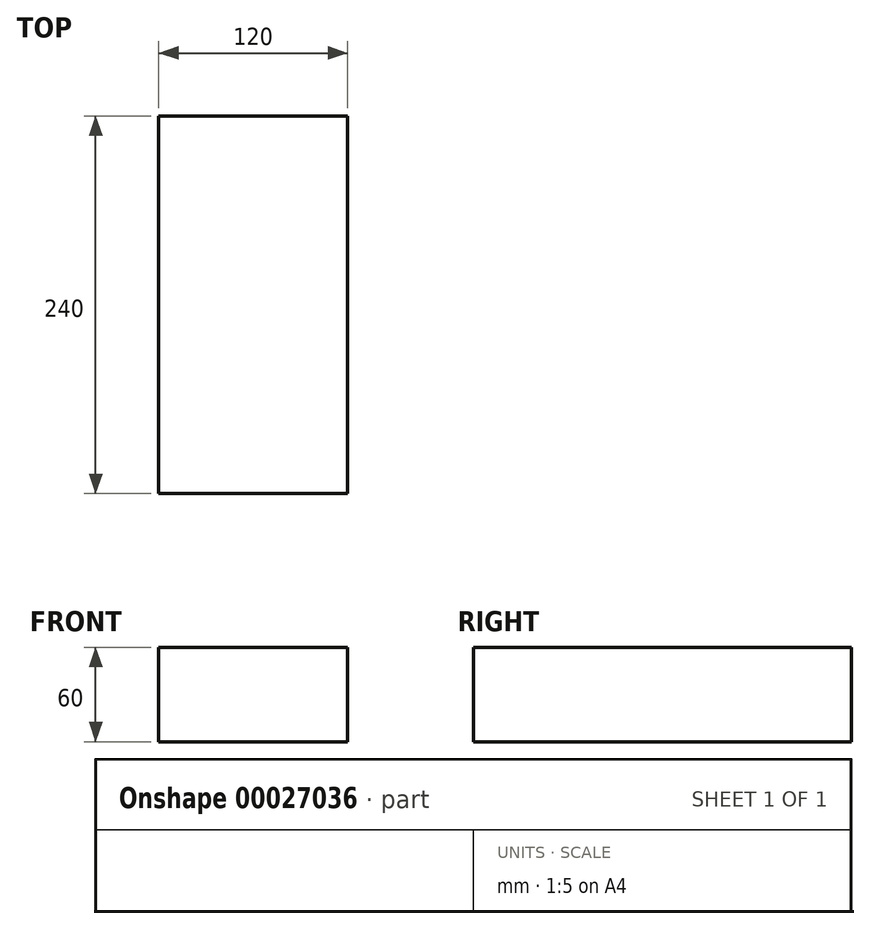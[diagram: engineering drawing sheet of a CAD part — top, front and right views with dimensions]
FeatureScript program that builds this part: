
annotation { "Feature Type Name" : "Feature", "Feature Type Description" : "" }
export const myFeature = defineFeature(function(context is Context, id is Id, definition is map)
    precondition{}
    {
        {
            var Q0;
            Q0=qCreatedBy(makeId("Front.planeOp"),FACE);
            var sketch = newSketch(context, id + "F0", { "sketchPlane" : qUnion([Q0])});
            skLineSegment(sketch, "E0.bottom", {"start": v(0, 0) * mm, "end": v(-120, 0) * mm});
            skLineSegment(sketch, "E0.top", {"start": v(0, -60) * mm, "end": v(-120, -60) * mm});
            skLineSegment(sketch, "E0.left", {"start": v(0, 0) * mm, "end": v(0, -60) * mm});
            skLineSegment(sketch, "E0.right", {"start": v(-120, 0) * mm, "end": v(-120, -60) * mm});
            skSolve(sketch);
        }
        {
            var Q0;
            Q0=makeQuery(id+"F0.imprint","IMPRINT",FACE,{"disambiguationData":[TD([[makeQuery(id+"F0.imprint","IMPRINT",EDGE,{"derivedFrom":sQuery(id+"F0.wireOp",EDGE,"E0.bottom")}),1.0]])]});
            extrude(context, id + "F1", {"entities" : qUnion([Q0]), "oppositeDirection" : true, "depth" : 240 * mm});
        }
    });
